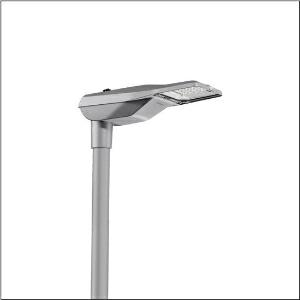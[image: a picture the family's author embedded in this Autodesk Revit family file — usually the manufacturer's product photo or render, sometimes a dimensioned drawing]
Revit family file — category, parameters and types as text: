
# Revit family: streetlight_sl_21_iq_micro___st1_0a_5xe1d31v08cb_77a3
name_source: partatom
category: Lighting Fixtures
units: mm (PartAtom-declared; Revit-internal decimal feet)

## family parameters
Cut with Voids When Loaded = No
Host = Face
Light Source = No
Part Type = Normal
Room Calculation Point = No
Round Connector Dimension = Use Diameter
Shared = No

## types (1)
- --- (1 x LED, 2880 lm, 19.1 W, 3000K)
    Apparent Load = 19 VA
    CIE Flux Codes = 37 72 97 100 100
    Color Rendering = 70
    Color Temperature = 3000K
    Default Elevation = 1800 mm
    Description = Streetlight SL 21 iQ micro, mast luminaire, primary light control with lens, of PMMA, primary optical cover: cover, of toughened safety glass, transparent, light distribution: ST1.0a, light emission: direct distribution, primary light characteristic: asymmetric, installation type: post-top, side-entry, LED, High Power LED, rated luminous flux: 2.880lm, luminous efficacy: 151lm/W, light colour: 730, colour temperature: 3000K, control gear: iQ-Street Remote, D4i with power reduction, control: pre-setting: logarithmic dimming characteristic, Street-Remote, Auto-Match, Temp-Guard, Lumen-Switch, Night-Set, Smart-Wire, Light-Fading, Desk-Remote (wireless, voltage-free reading and setting of iQ features in the workshop via application-optimized NFC function/RFID function), optimised constant luminous flux control (CLO 2.0), mains connection: 220..240V, AC, 50/60Hz, start of lifetime: 19W, end of service life: 20W, reduction: 9W, luminaire housing, of diecast aluminium, powder-coated, SITECO metallic grey (DB 702S), corrosivity category C5 high according to DIN EN ISO 12944, please order mast flange separately, inclination adjustable: 0°, 5°, 10°, 15°, sealing non-destructively replaceable, multi-level sealing system, length: 528mm, width: 235mm, height: 110mm, mast flange for spigot size: 42mm (side-entry): 5XC10008XM4, 60/48mm (side-entry/post-top): 5XC10108XM2, 76/60mm (side-entry/post-top): 5XC10108XM1, mounting height: 4..8m, Smart Interface above, protection rating (complete): IP66, insulation class (complete): insulation class II (safety insulation), certification: CE, ENEC, ENEC+, VDE, impact resistance: IK10, permissible operating ambient temperature for outdoor applications: -40..+50°C, standard-compliant lighting for roads and squares, packaging unit: 1 piece

Light Distribution: ST1.0a
    Height = 110 mm
    Lamp = 1 x LED
    Lamp Light Flux = 2880 lm
    Lamp Power = 19.1 W
    Lamp count = 1
    Length = 528 mm
    Luminous efficacy = 151 lm/W
    Manufacturer = Siteco
    ModVariant = No
    Model = 5XE1D31V08CB
    Mounting Place = Pole
    Mounting Type = Pole top
    Number of Poles = 1
    OnlyDefault = Yes
    Power Factor = 1
    Product Name = Streetlight SL 21 iQ micro | ST1.0a
    Product group = mast luminaire | pylon top
    ProductGroupID = 6100
    Protection Class = Protection class II
    Protection Degree = IP 66
    RLX_Detail_Level = 1
    RLX_Emergency_Light_Flux = 0 lm
    RLX_Emergency_Type = 0
    RLX_Emergency_Type_DB = No
    RlxData = <blob elided: 98369 chars, md5=418d0ff7>
    Socket = socket
    Standby Power = 0 W
    System Light Flux = 2880 lm
    System Power = 19 W
    Type Comments = factory setting: luminous flux: 100 % | dim-lin: 254 | 387 mA
    Type Image = l_1277292.jpg
    URL = http://relux.com
    VarID = @adj_117363
    Voltage = 0 V
    Weight = 0.00 kg
    Width = 235 mm

## geometry (parser evidence)
native form markers: Blend x4, Sweep x13
no freeform markers — native parametric forms only
